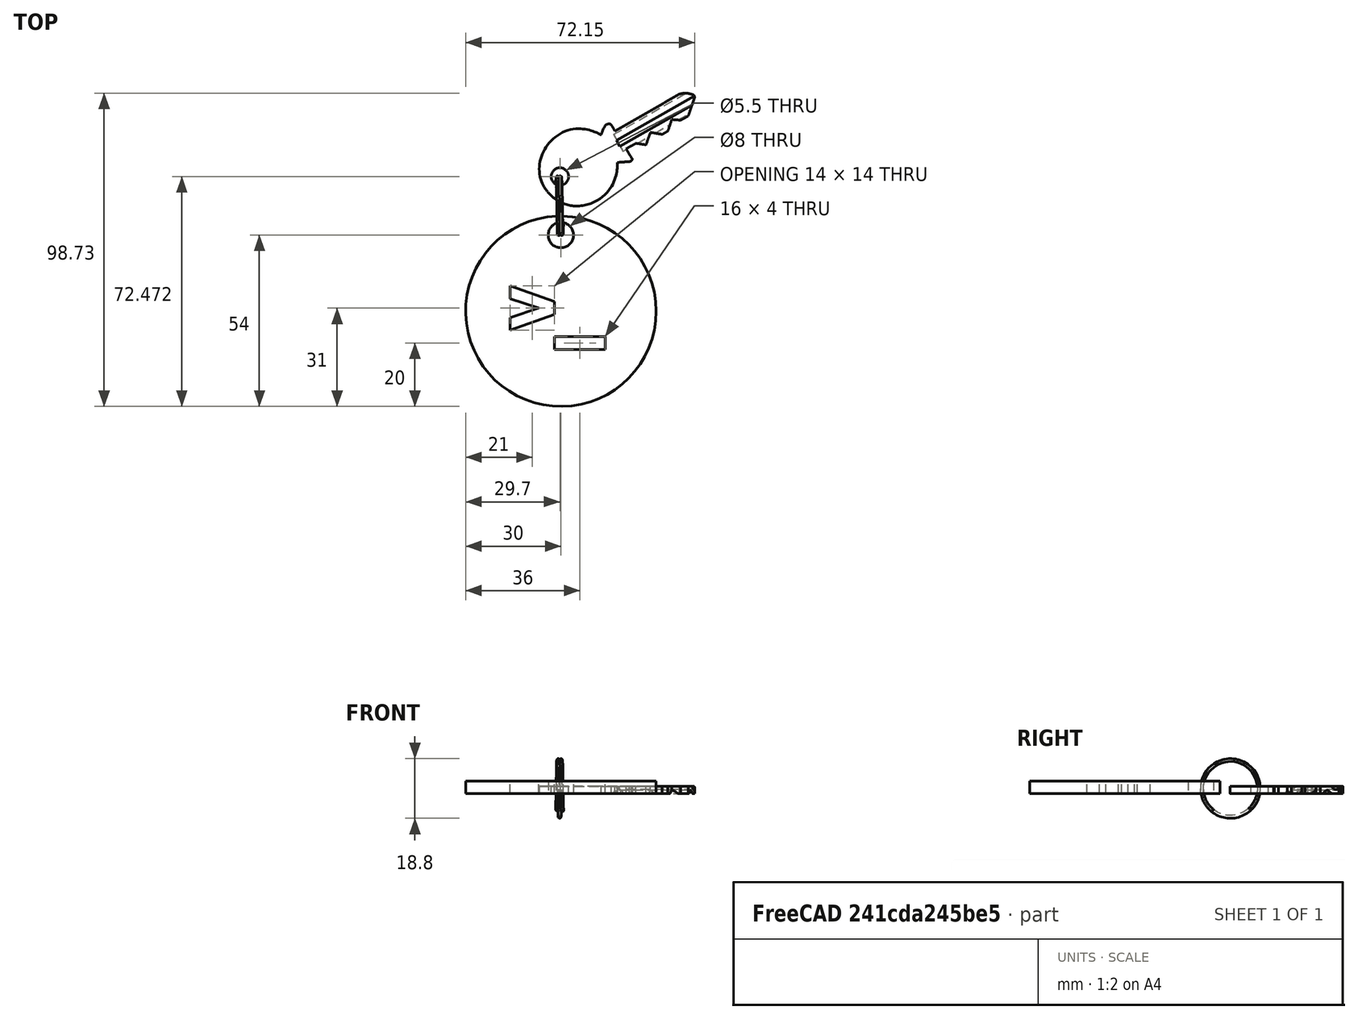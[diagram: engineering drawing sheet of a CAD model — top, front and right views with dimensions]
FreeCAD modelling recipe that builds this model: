
FCSTD DOCUMENT  (FreeCAD 0.16RUnknown)
Label: Terminal
License: CreativeCommons Attribution-ShareAlike
LicenseURL: http://creativecommons.org/licenses/by-sa/4.0/
objects: Part::Feature×2, Sketcher::SketchObject×1, PartDesign::Pad×1, App::DocumentObjectGroup×1
note: 5 computed .brp shape members not serialized (recipe doc carries the construction recipe); baked Part::Feature solids carry a one-line shape summary decoded from their .brp

FEATURE [Part::Feature] Sweep  label="key-ring-model-1"
  Placement = pos=(-1.2,30.2546,1.6391) rot=(0.333333,0.881918,0.333333;1.69612rad)
  shape: bbox 3.31 x 27.02 x 26.33 mm, 4 faces (baked)
FEATURE [Part::Feature] Cut  label="key-model-1"
  Placement = pos=(-5.46976,36.5266,0) rot=(0,0,1;0.517888rad)
  shape: bbox 49.82 x 36.6 x 2.3 mm, 44 faces (baked)
FEATURE [Sketcher::SketchObject] Sketch001
  Placement = pos=(-30,-33,0) rot=(0,0,1;0rad)
  sketch-geometry (16):
    g0: Circle CenterX=30 CenterY=30 CenterZ=0 NormalX=0 NormalY=0 NormalZ=1 Radius=30
    g1: LineSegment StartX=28 StartY=22 StartZ=0 EndX=44 EndY=22 EndZ=0
    g2: LineSegment StartX=44 StartY=22 StartZ=0 EndX=44 EndY=18 EndZ=0
    g3: LineSegment StartX=44 StartY=18 StartZ=0 EndX=28 EndY=18 EndZ=0
    g4: LineSegment StartX=28 StartY=18 StartZ=0 EndX=28 EndY=22 EndZ=0
    g5: LineSegment StartX=14 StartY=38 StartZ=0 EndX=28 EndY=33 EndZ=0
    g6: LineSegment StartX=28 StartY=33 StartZ=0 EndX=28 EndY=29 EndZ=0
    g7: LineSegment StartX=28 StartY=29 StartZ=0 EndX=14 EndY=24 EndZ=0
    g8: LineSegment StartX=14 StartY=24 StartZ=0 EndX=14 EndY=28 EndZ=0
    g9: LineSegment StartX=14 StartY=28 StartZ=0 EndX=23 EndY=31 EndZ=0
    g10: LineSegment StartX=23 StartY=31 StartZ=0 EndX=14 EndY=34 EndZ=0
    g11: LineSegment StartX=14 StartY=34 StartZ=0 EndX=14 EndY=38 EndZ=0
    g12: LineSegment [constr] StartX=14 StartY=34 StartZ=0 EndX=14 EndY=28 EndZ=0
    g13: LineSegment [constr] StartX=23 StartY=31 StartZ=0 EndX=28 EndY=31 EndZ=0
    g14: Circle CenterX=30 CenterY=54 CenterZ=0 NormalX=0 NormalY=0 NormalZ=1 Radius=4
    g15: LineSegment [constr] StartX=30 StartY=54 StartZ=0 EndX=30 EndY=30 EndZ=0
  constraints (45):
    c: Tangent(g-1,g0)
    c: Tangent(g0,g-2)
    c: Radius(g0) = 30
    c: Coincident(g1,g2)
    c: Coincident(g2,g3)
    c: Coincident(g3,g4)
    c: Coincident(g4,g1)
    c: Horizontal(g1)
    c: Horizontal(g3)
    c: Vertical(g2)
    c: Vertical(g4)
    c: DistanceY(g-1,g3) = 18
    c: DistanceX(g-1,g3) = 28
    c: DistanceX(g1,g1) = 16
    c: DistanceY(g2,g2) = 4
    c: Coincident(g5,g6)
    c: Vertical(g6)
    c: Coincident(g6,g7)
    c: Coincident(g7,g8)
    c: Vertical(g8)
    c: Coincident(g8,g9)
    c: Coincident(g9,g10)
    c: Coincident(g10,g11)
    c: Coincident(g11,g5)
    c: Vertical(g11)
    c: Coincident(g12,g8)
    c: Coincident(g12,g10)
    c: Vertical(g12)
    c: DistanceX(g5,g9) = 9
    c: Distance(g5,g11) = 14
    c: DistanceX(g-1,g7) = 14
    c: Coincident(g9,g13)
    c: PointOnObject(g13,g6)
    c: Symmetric(g5,g6,g13)
    c: DistanceY(g-1,g9) = 31
    c: DistanceY(g6,g6) = 4
    c: Symmetric(g5,g7,g13)
    c: Equal(g8,g6)
    c: DistanceY(g8,g10) = 6
    c: Equal(g11,g8)
    c: Coincident(g15,g14)
    c: Coincident(g15,g0)
    c: Vertical(g15)
    c: Radius(g14) = 4
    c: DistanceY(g15,g15) = 24
FEATURE [PartDesign::Pad] Pad
  Length = 4
  Length2 = 100
  Placement = pos=(-30,-33,0) rot=(0,0,1;0rad)
  Sketch = -> Sketch001
  Type = 0
FEATURE [App::DocumentObjectGroup] Group  label="Assembly"
  Group = -> [Sweep,Cut,Pad]
